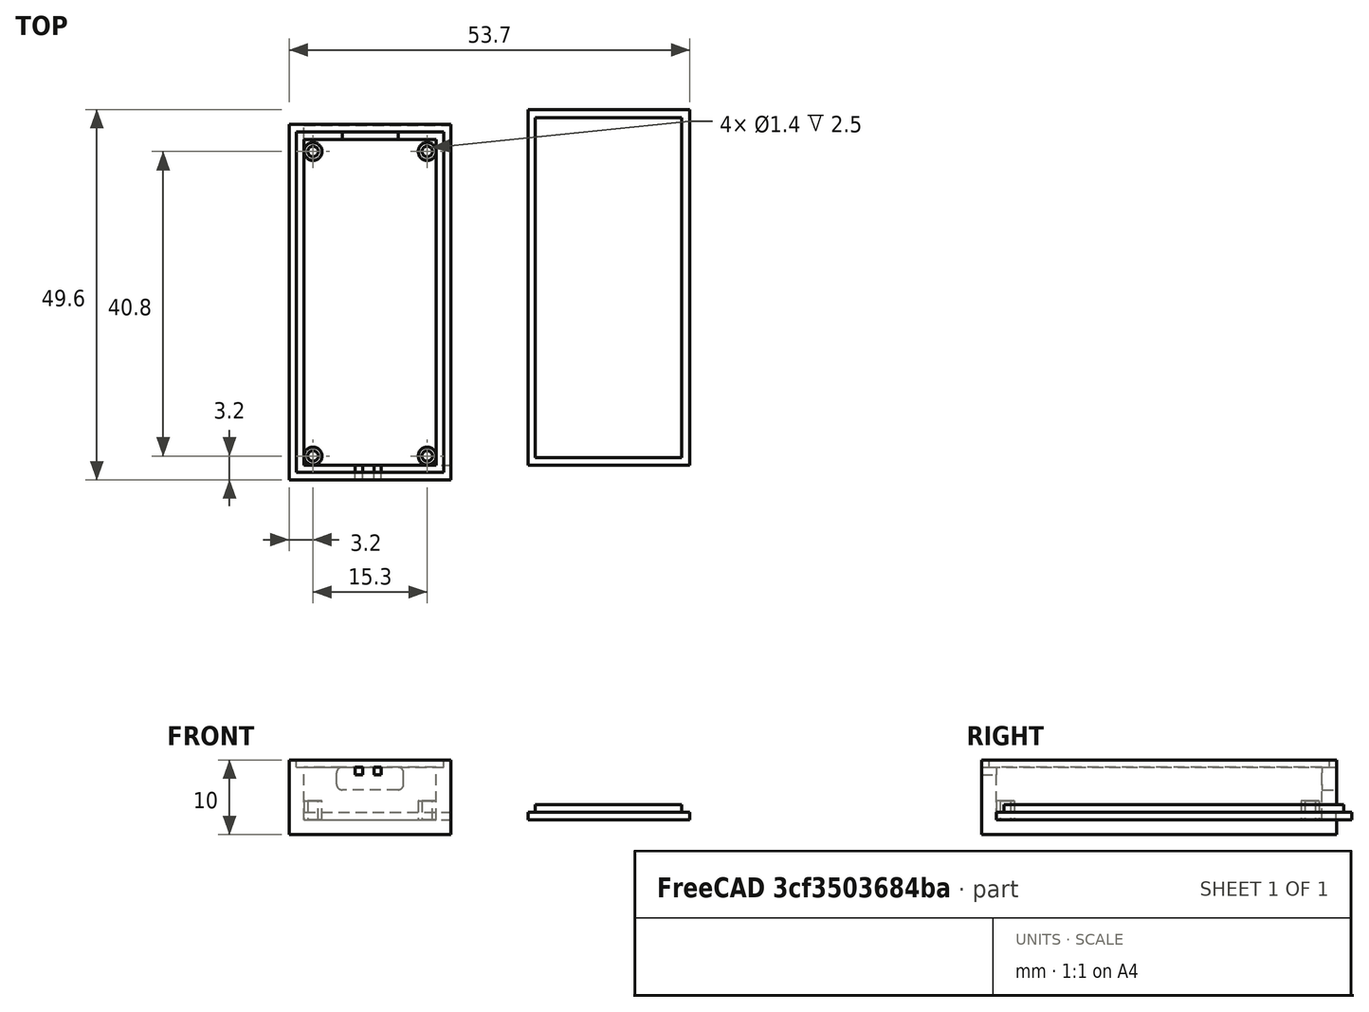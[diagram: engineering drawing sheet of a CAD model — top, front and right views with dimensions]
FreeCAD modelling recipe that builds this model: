
FCSTD DOCUMENT  (FreeCAD 1.0R39109 (Git))
Label: IRSender
License: All rights reserved
LicenseURL: https://en.wikipedia.org/wiki/All_rights_reserved
objects: Part::Box×8, PartDesign::Fillet×4, Part::Cut×4, Part::MultiFuse×3, Sketcher::SketchObject×2, Part::Extrusion×2, PartDesign::FeatureBase×2, PartDesign::Body×2
note: 39 computed .brp shape members not serialized (recipe doc carries the construction recipe); baked Part::Feature solids carry a one-line shape summary decoded from their .brp

FEATURE [Part::Box] Box  label="Base"
  AttacherType = Attacher::AttachEngine3D
  Height = 2
  Length = 17.7
  Placement = pos=(0,0,-2) rot=(0,0,1;0rad)
  Width = 43.6
FEATURE [Sketcher::SketchObject] Sketch
  ArcFitTolerance = 1e-06
  FullyConstrained = true
  MakeInternals = false
  sketch-geometry (8):
    g0: Circle CenterX=16.5 CenterY=1.2 CenterZ=0 NormalX=0 NormalY=0 NormalZ=1 AngleXU=0 Radius=0.7
    g1: Circle CenterX=16.5 CenterY=1.2 CenterZ=0 NormalX=0 NormalY=0 NormalZ=1 AngleXU=0 Radius=1.2
    g2: Circle CenterX=1.2 CenterY=1.2 CenterZ=0 NormalX=0 NormalY=0 NormalZ=1 AngleXU=0 Radius=0.7
    g3: Circle CenterX=1.2 CenterY=1.2 CenterZ=0 NormalX=0 NormalY=0 NormalZ=1 AngleXU=0 Radius=1.2
    g4: Circle CenterX=1.2 CenterY=42 CenterZ=0 NormalX=0 NormalY=0 NormalZ=1 AngleXU=0 Radius=0.7
    g5: Circle CenterX=1.2 CenterY=42 CenterZ=0 NormalX=0 NormalY=0 NormalZ=1 AngleXU=0 Radius=1.2
    g6: Circle CenterX=16.5 CenterY=42 CenterZ=0 NormalX=0 NormalY=0 NormalZ=1 AngleXU=0 Radius=0.7
    g7: Circle CenterX=16.5 CenterY=42 CenterZ=0 NormalX=0 NormalY=0 NormalZ=1 AngleXU=0 Radius=1.2
  constraints (20):
    c: Diameter(g0) = 1.4
    c: Diameter(g1) = 2.4
    c: Coincident(g1,g0)
    c: Diameter(g2) = 1.4
    c: Diameter(g3) = 2.4
    c: Coincident(g3,g2)
    c: Horizontal(g2,g0)
    c: Diameter(g4) = 1.4
    c: Diameter(g5) = 2.4
    c: Coincident(g5,g4)
    c: Diameter(g6) = 1.4
    c: Diameter(g7) = 2.4
    c: Coincident(g7,g6)
    c: Vertical(g6,g0)
    c: Horizontal(g4,g6)
    c: Vertical(g4,g2)
    c: DistanceX(g4,g6) = 15.3
    c: DistanceY(g0,g6) = 40.8
    c: Distance(g2,g-1) = 1.2
    c: Distance(g2,g-2) = 1.2
FEATURE [Part::Extrusion] Extrude
  Base = -> Sketch
  Dir = (0,0,1)
  DirMode = 2
  FaceMakerClass = Part::FaceMakerBullseye
  FaceMakerMode = 3
  LengthFwd = 2.5
  LengthRev = 0
  Solid = true
  Symmetric = false
FEATURE [Part::MultiFuse] Fusion  label="Arduino Mount"
  Shapes = -> [Extrude,Box]
FEATURE [Sketcher::SketchObject] Sketch001
  ArcFitTolerance = 1e-06
  FullyConstrained = true
  MakeInternals = false
  sketch-geometry (8):
    g0: LineSegment StartX=-2 StartY=-2 StartZ=0 EndX=19.7 EndY=-2 EndZ=0
    g1: LineSegment StartX=19.7 StartY=-2 StartZ=0 EndX=19.7 EndY=45.6 EndZ=0
    g2: LineSegment StartX=19.7 StartY=45.6 StartZ=0 EndX=-2 EndY=45.6 EndZ=0
    g3: LineSegment StartX=-2 StartY=45.6 StartZ=0 EndX=-2 EndY=-2 EndZ=0
    g4: LineSegment StartX=0 StartY=0 StartZ=0 EndX=17.7 EndY=0 EndZ=0
    g5: LineSegment StartX=17.7 StartY=0 StartZ=0 EndX=17.7 EndY=43.6 EndZ=0
    g6: LineSegment StartX=17.7 StartY=43.6 StartZ=0 EndX=0 EndY=43.6 EndZ=0
    g7: LineSegment StartX=0 StartY=43.6 StartZ=0 EndX=0 EndY=0 EndZ=0
  constraints (23):
    c: Coincident(g0,g1)
    c: Coincident(g1,g2)
    c: Coincident(g2,g3)
    c: Coincident(g3,g0)
    c: Horizontal(g0)
    c: Horizontal(g2)
    c: Vertical(g1)
    c: Vertical(g3)
    c: Coincident(g4,g5)
    c: Coincident(g5,g6)
    c: Coincident(g6,g7)
    c: Coincident(g7,g4)
    c: Horizontal(g4)
    c: Horizontal(g6)
    c: Vertical(g5)
    c: Vertical(g7)
    c: Coincident(g4,g-1)
    c: DistanceX(g6,g6) = 17.7
    c: DistanceY(g5,g5) = 43.6
    c: Distance(g1,g5) = 2
    c: Distance(g0,g4) = 2
    c: Distance(g3,g7) = 2
    c: Distance(g6,g2) = 2
FEATURE [Part::Extrusion] Extrude001  label="Walls"
  Base = -> Sketch001
  Dir = (0,0,1)
  DirMode = 2
  FaceMakerClass = Part::FaceMakerBullseye
  FaceMakerMode = 3
  LengthFwd = 10
  LengthRev = 0
  Placement = pos=(0,0,-2) rot=(0,0,1;0rad)
  Solid = true
  Symmetric = false
FEATURE [Part::Box] Box002  label="Port Cutout"
  AttacherType = Attacher::AttachEngine3D
  Height = 3
  Length = 9
  Placement = pos=(4.35,-3,4) rot=(0,0,1;0rad)
  Width = 4
FEATURE [PartDesign::FeatureBase] BaseFeature
  BaseFeature = -> Box002
  Suppressed = false
FEATURE [PartDesign::Fillet] Fillet
  Base = -> BaseFeature [Edge6]
  BaseFeature = -> BaseFeature
  Radius = 0.75
  Refine = true
  SupportTransform = false
  Suppressed = false
  UseAllEdges = false
FEATURE [PartDesign::Fillet] Fillet001
  Base = -> Fillet [Edge15]
  BaseFeature = -> Fillet
  Radius = 0.75
  Refine = true
  SupportTransform = false
  Suppressed = false
  UseAllEdges = false
FEATURE [PartDesign::Fillet] Fillet002
  Base = -> Fillet001 [Edge14]
  BaseFeature = -> Fillet001
  Radius = 0.75
  Refine = true
  SupportTransform = false
  Suppressed = false
  UseAllEdges = false
FEATURE [PartDesign::Fillet] Fillet003
  Base = -> Fillet002 [Edge16]
  BaseFeature = -> Fillet002
  Radius = 0.75
  Refine = true
  SupportTransform = false
  Suppressed = false
  UseAllEdges = false
FEATURE [PartDesign::Body] Body001  label="Port Cutout Fancy"
  AllowCompound = false
  BaseFeature = -> Box002
  Group = -> [BaseFeature,Fillet,Fillet001,Fillet002,Fillet003]
  Origin = -> Origin001
  Placement = pos=(4.35,42,4) rot=(0,0,1;0rad)
  Tip = -> Fillet003
FEATURE [Part::Cut] Cut  label="Wall with cutout"
  Base = -> Extrude001
  Tool = -> Body001
FEATURE [Part::MultiFuse] Fusion001  label="Arduino Box"
  Shapes = -> [Cut,Fusion]
FEATURE [Part::Box] Box003  label="Lid Cutout"
  AttacherType = Attacher::AttachEngine3D
  Height = 1
  Length = 19.7
  Placement = pos=(-1,-1,7) rot=(0,0,1;0rad)
  Width = 45.6
FEATURE [Part::Cut] Cut001  label="Box with lid cutout"
  Base = -> Fusion001
  Tool = -> Box003
FEATURE [Part::Box] Box004  label="Cube001"
  AttacherType = Attacher::AttachEngine3D
  Height = 1
  Length = 19.6
  Placement = pos=(-1,-1,7) rot=(0,0,1;0rad)
  Width = 45.5
FEATURE [PartDesign::FeatureBase] BaseFeature001
  BaseFeature = -> Box004
  Suppressed = false
FEATURE [PartDesign::Body] Body
  AllowCompound = false
  BaseFeature = -> Box004
  Group = -> [BaseFeature001]
  Origin = -> Origin
  Tip = -> BaseFeature001
FEATURE [Part::Box] Box006  label="Cube"
  AttacherType = Attacher::AttachEngine3D
  Height = 1
  Length = 19.6
  Placement = pos=(1,1,1) rot=(0,0,1;0rad)
  Width = 45.5
FEATURE [Part::Box] Box007  label="Cube003"
  AttacherType = Attacher::AttachEngine3D
  Height = 1
  Length = 21.7
  Width = 47.6
FEATURE [Part::MultiFuse] Fusion002  label="Lid"
  Placement = pos=(30,0,0) rot=(0,0,1;0rad)
  Shapes = -> [Box006,Box007]
FEATURE [Part::Box] Box008  label="Cube004"
  AttacherType = Attacher::AttachEngine3D
  Height = 1
  Length = 1
  Placement = pos=(6.85,-2.5,6) rot=(0,0,1;0rad)
  Width = 3
FEATURE [Part::Box] Box009  label="Cube005"
  AttacherType = Attacher::AttachEngine3D
  Height = 1
  Length = 1
  Placement = pos=(9.35,-2.5,6) rot=(0,0,1;0rad)
  Width = 3
FEATURE [Part::Cut] Cut002
  Base = -> Cut001
  Tool = -> Box008
FEATURE [Part::Cut] Cut003  label="Box with LED cutout"
  Base = -> Cut002
  Tool = -> Box009
